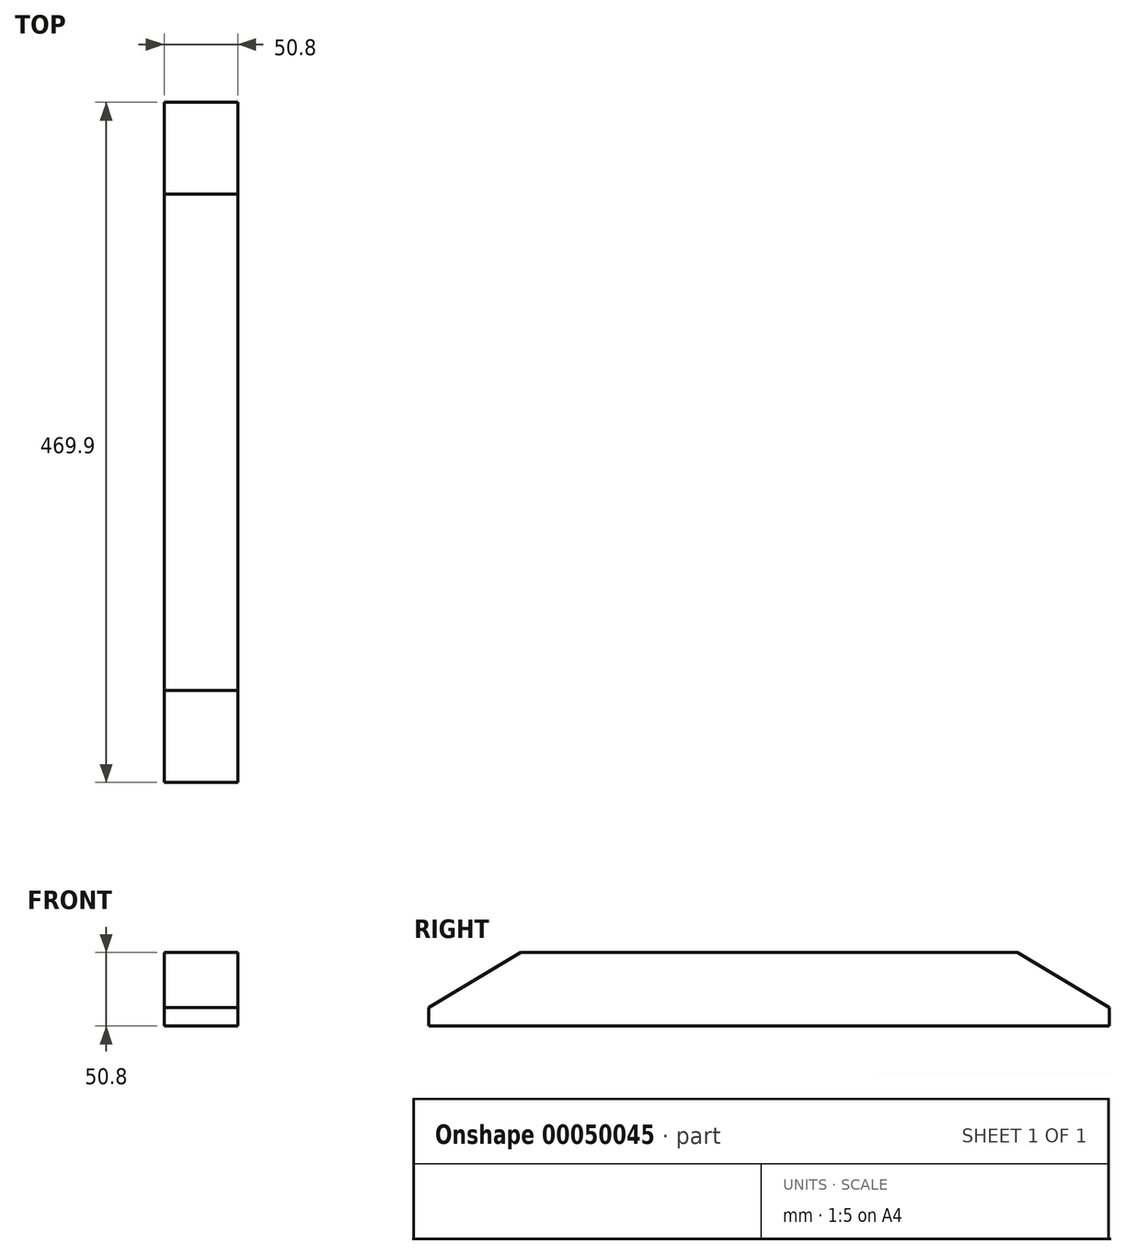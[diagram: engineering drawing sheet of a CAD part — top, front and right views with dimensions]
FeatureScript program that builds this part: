
annotation { "Feature Type Name" : "Feature", "Feature Type Description" : "" }
export const myFeature = defineFeature(function(context is Context, id is Id, definition is map)
    precondition{}
    {
        {
            var Q0;
            Q0=qCreatedBy(makeId("Top.planeOp"),FACE);
            var sketch = newSketch(context, id + "F0", { "sketchPlane" : qUnion([Q0])});
            skLineSegment(sketch, "E0.bottom", {"start": v(0, 0) * mm, "end": v(50.8, 0) * mm});
            skLineSegment(sketch, "E0.top", {"start": v(0, 469.9) * mm, "end": v(50.8, 469.9) * mm});
            skLineSegment(sketch, "E0.left", {"start": v(0, 0) * mm, "end": v(0, 469.9) * mm});
            skLineSegment(sketch, "E0.right", {"start": v(50.8, 0) * mm, "end": v(50.8, 469.9) * mm});
            skSolve(sketch);
        }
        {
            var Q0;
            Q0=makeQuery(id+"F0.imprint","IMPRINT",FACE,{"disambiguationData":[TD([[makeQuery(id+"F0.imprint","IMPRINT",EDGE,{"derivedFrom":sQuery(id+"F0.wireOp",EDGE,"E0.bottom")}),1.0]])]});
            extrude(context, id + "F1", {"entities" : qUnion([Q0]), "depth" : 50.8 * mm});
        }
        {
            var Q0;
            Q0=makeQuery(id+"F1.opExtrude","SWEPT_FACE",FACE,{"disambiguationData":[OSD([sQuery(id+"F0.wireOp",EDGE,"E0.right")])]});
            var sketch = newSketch(context, id + "F2", { "sketchPlane" : qUnion([Q0])});
            skLineSegment(sketch, "E1", {"start": v(0, 0) * mm, "end": v(0, 12.7) * mm});
            skLineSegment(sketch, "E2", {"start": v(0, 12.7) * mm, "end": v(63.5, 50.8) * mm});
            skLineSegment(sketch, "E3", {"start": v(63.5, 50.8) * mm, "end": v(0, 50.8) * mm});
            skLineSegment(sketch, "E4", {"start": v(0, 50.8) * mm, "end": v(0, 12.7) * mm});
            skLineSegment(sketch, "E5", {"start": v(469.9, 0) * mm, "end": v(469.9, 12.7) * mm});
            skLineSegment(sketch, "E6", {"start": v(469.9, 12.7) * mm, "end": v(406.4, 50.8) * mm});
            skLineSegment(sketch, "E7", {"start": v(406.4, 50.8) * mm, "end": v(469.9, 50.8) * mm});
            skLineSegment(sketch, "E8", {"start": v(469.9, 50.8) * mm, "end": v(469.9, 12.7) * mm});
            skSolve(sketch);
        }
        {
            var Q0;
            Q0=makeQuery(id+"F2.imprint","IMPRINT",FACE,{"disambiguationData":[TD([[makeQuery(id+"F2.imprint","IMPRINT",EDGE,{"derivedFrom":sQuery(id+"F2.wireOp",EDGE,"E2")}),1.0]])]});
            var Q1;
            Q1=makeQuery(id+"F2.imprint","IMPRINT",FACE,{"disambiguationData":[TD([[makeQuery(id+"F2.imprint","IMPRINT",EDGE,{"derivedFrom":sQuery(id+"F2.wireOp",EDGE,"E6")}),-1.0]])]});
            extrude(context, id + "F3", {"entities" : qUnion([Q0, Q1]), "operationType" : NewBodyOperationType.REMOVE, "endBound" : BoundingType.THROUGH_ALL, "oppositeDirection" : true, "depth" : 25.4 * mm});
        }
    });
